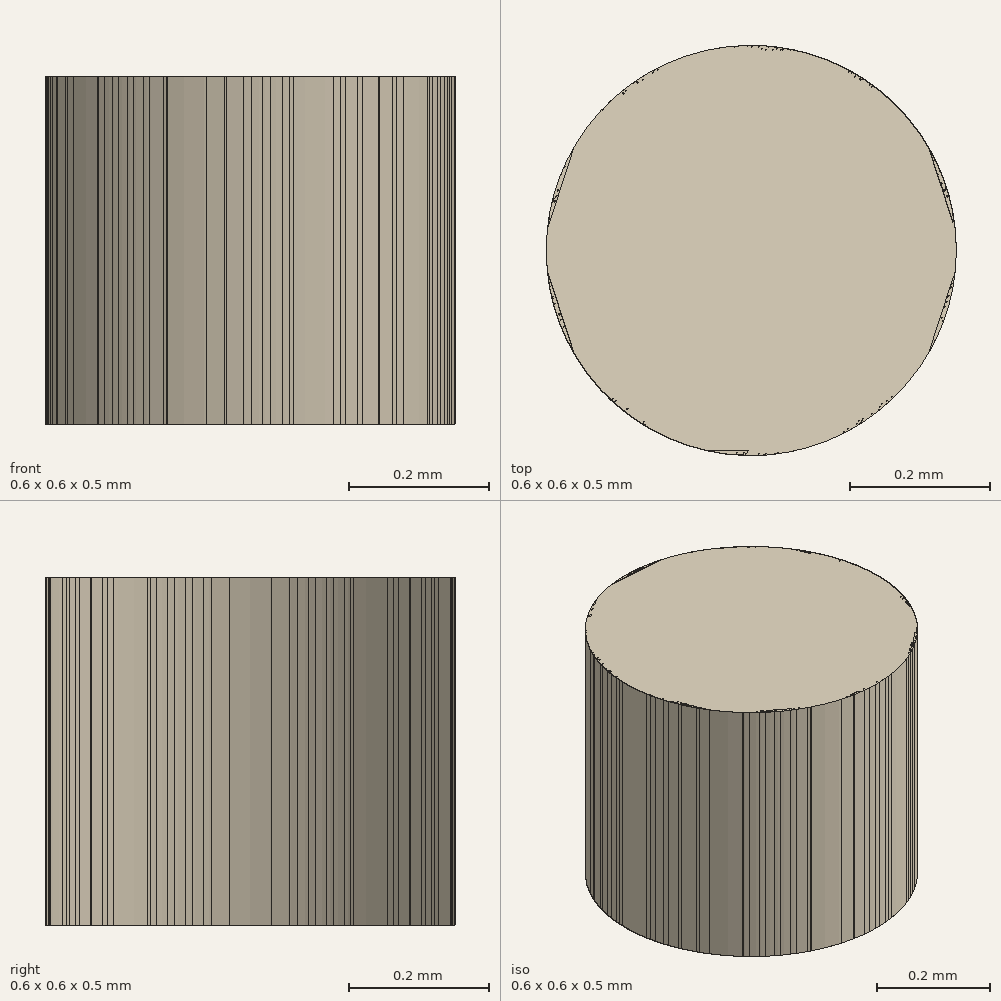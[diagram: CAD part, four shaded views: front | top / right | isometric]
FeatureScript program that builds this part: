
annotation { "Feature Type Name" : "Feature", "Feature Type Description" : "" }
export const myFeature = defineFeature(function(context is Context, id is Id, definition is map)
    precondition{}
    {
        {
            var Q0;
            Q0=qCreatedBy(makeId("Top.planeOp"),FACE);
            var sketch = newSketch(context, id + "F0", { "sketchPlane" : qUnion([Q0])});
            skCircle(sketch, "E0", {"center": v(0, 0) * mm, "radius": 0.3 * mm});
            skCircle(sketch, "E1", {"center": v(0, 0) * mm, "radius": 0.5 * mm, "construction": true});
            skCircle(sketch, "E2", {"center": v(0, 0) * mm, "radius": 0.58 * mm, "construction": true});
            skLineSegment(sketch, "E3", {"start": v(-0.06, 0.5) * mm, "end": v(0.06, 0.5) * mm, "construction": true});
            skLineSegment(sketch, "E4", {"start": v(0, 0) * mm, "end": v(0, 0.58) * mm, "construction": true});
            skPoint(sketch, "E5", {"position": v(0, 0.5) * mm});
            skCircle(sketch, "E6", {"center": v(0, 0.58) * mm, "radius": 0.08 * mm, "construction": true});
            skCircle(sketch, "E7", {"center": v(-0.06, 0.5) * mm, "radius": 0.08 * mm, "construction": true});
            skCircle(sketch, "E8", {"center": v(0.06, 0.5) * mm, "radius": 0.08 * mm, "construction": true});
            skArc(sketch, "E9", {"start": v(-0.06, 0.5) * mm, "mid": v(-0.05, 0.55) * mm, "end": v(0, 0.58) * mm});
            skArc(sketch, "E10", {"start": v(0.06, 0.5) * mm, "mid": v(0.05, 0.55) * mm, "end": v(0, 0.58) * mm});
            skLineSegment(sketch, "E11", {"start": v(-0.06, 0.5) * mm, "end": v(-0.06, 0.29) * mm});
            skLineSegment(sketch, "E12", {"start": v(-0.06, 0.29) * mm, "end": v(0.06, 0.29) * mm});
            skLineSegment(sketch, "E13", {"start": v(0.06, 0.29) * mm, "end": v(0.06, 0.5) * mm});
            skSolve(sketch);
        }
        {
            var Q0;
            Q0=makeQuery(id+"F0.imprint","IMPRINT",FACE,{"disambiguationData":[TD([[makeQuery(id+"F0.imprint","IMPRINT",EDGE,{"derivedFrom":sQuery(id+"F0.wireOp",EDGE,"E9")}),-1.0]])]});
            var Q1;
            {var subQ0=sQuery(id+"F0.wireOp",EDGE,"E12");Q1=makeQuery(id+"F0.imprint","IMPRINT",FACE,{"disambiguationData":[TD([[makeQuery(id+"F0.imprint","IMPRINT",EDGE,{"derivedFrom":subQ0}),1.0]])]});}
            extrude(context, id + "F1", {"entities" : qUnion([Q0, Q1]), "depth" : 0.5 * mm});
        }
        {
            var Q0;
            Q0=makeQuery(id+"F1.opExtrude","SWEPT_BODY",BODY,{"disambiguationData":[OSD([sQuery(id+"F0.wireOp",EDGE,"E9"),sQuery(id+"F0.wireOp",EDGE,"E10"),sQuery(id+"F0.wireOp",EDGE,"E11"),sQuery(id+"F0.wireOp",EDGE,"E12"),sQuery(id+"F0.wireOp",EDGE,"E13")])]});
            var Q1;
            Q1=sQuery(id+"F0.wireOp",EDGE,"E0");
            circularPattern(context, id + "F2", {"entities" : qUnion([Q0]), "axis" : qUnion([Q1]), "angle" : 36 * degree, "instanceCount" : 10});
        }
        {
            var Q0;
            {var subQ0=sQuery(id+"F0.wireOp",EDGE,"E12");Q0=makeQuery(id+"F0.imprint","IMPRINT",FACE,{"disambiguationData":[TD([[makeQuery(id+"F0.imprint","IMPRINT",EDGE,{"derivedFrom":subQ0}),-1.0]])]});}
            var Q1;
            {var subQ0=sQuery(id+"F0.wireOp",EDGE,"E12");Q1=makeQuery(id+"F0.imprint","IMPRINT",FACE,{"disambiguationData":[TD([[makeQuery(id+"F0.imprint","IMPRINT",EDGE,{"derivedFrom":subQ0}),1.0]])]});}
            extrude(context, id + "F3", {"entities" : qUnion([Q0, Q1]), "depth" : 0.5 * mm});
        }
    });
